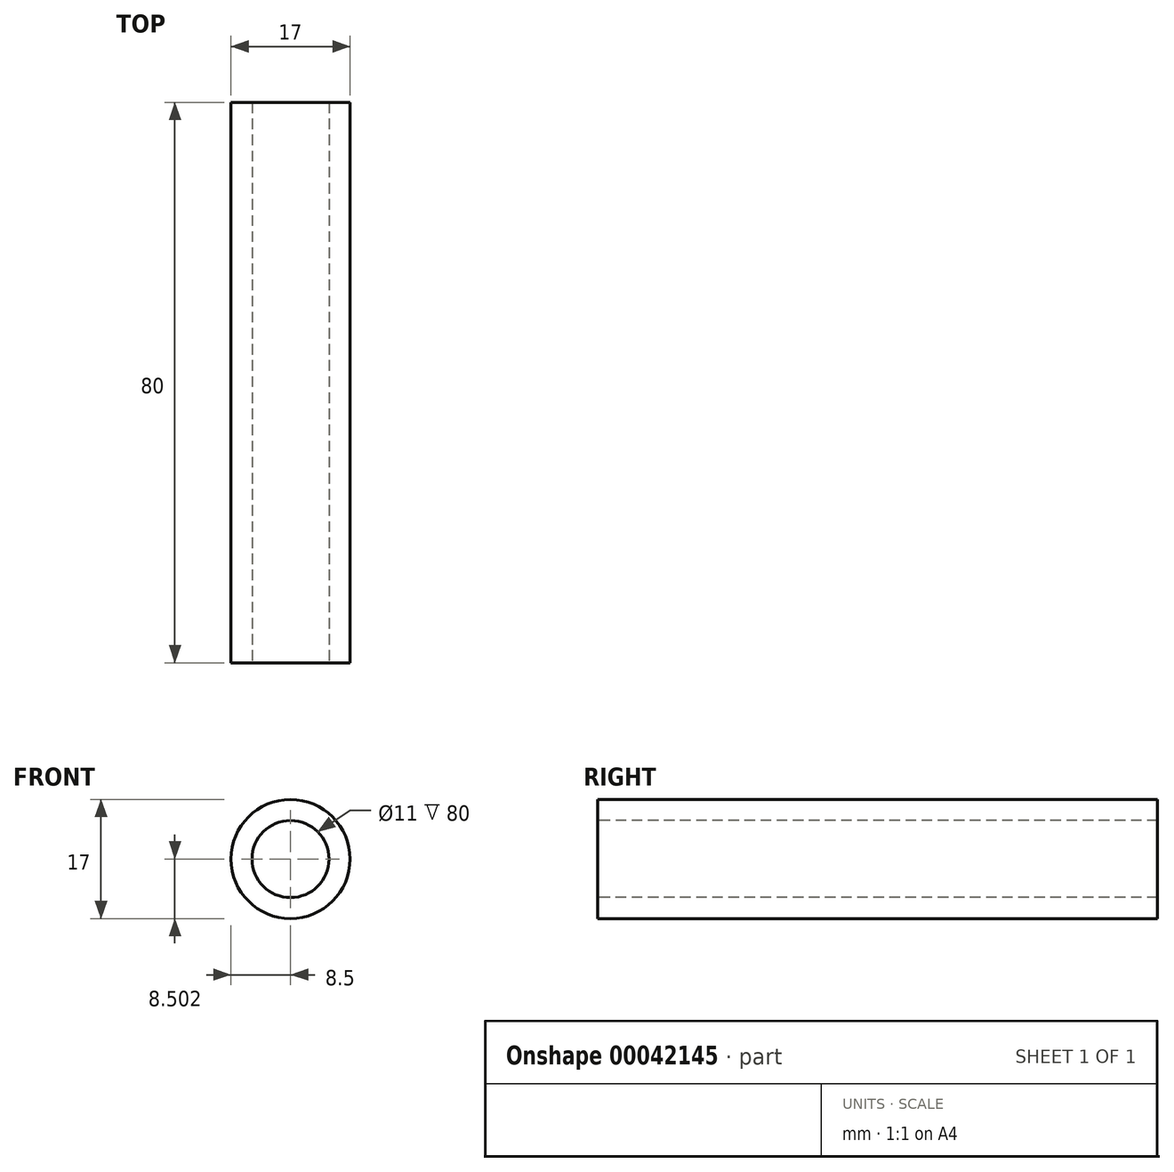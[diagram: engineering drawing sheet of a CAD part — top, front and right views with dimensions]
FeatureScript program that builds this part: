
annotation { "Feature Type Name" : "Feature", "Feature Type Description" : "" }
export const myFeature = defineFeature(function(context is Context, id is Id, definition is map)
    precondition{}
    {
        {
            var Q0;
            Q0=qCreatedBy(makeId("Right.planeOp"),FACE);
            var sketch = newSketch(context, id + "F0", { "sketchPlane" : qUnion([Q0])});
            skLineSegment(sketch, "E0", {"start": v(0, -16.48) * mm, "end": v(78.42, -16.48) * mm, "construction": true});
            skLineSegment(sketch, "E1.bottom", {"start": v(0, -7.98) * mm, "end": v(80, -7.98) * mm});
            skLineSegment(sketch, "E1.top", {"start": v(0, -10.98) * mm, "end": v(80, -10.98) * mm});
            skLineSegment(sketch, "E1.left", {"start": v(0, -7.98) * mm, "end": v(0, -10.98) * mm});
            skLineSegment(sketch, "E1.right", {"start": v(80, -7.98) * mm, "end": v(80, -10.98) * mm});
            skLineSegment(sketch, "E2.MirrorCS", {"start": v(80, -24.98) * mm, "end": v(80, -21.98) * mm});
            skLineSegment(sketch, "E3.MirrorCS", {"start": v(0, -24.98) * mm, "end": v(0, -21.98) * mm});
            skLineSegment(sketch, "E4.MirrorCS", {"start": v(0, -21.98) * mm, "end": v(80, -21.98) * mm});
            skLineSegment(sketch, "E5.MirrorCS", {"start": v(0, -24.98) * mm, "end": v(80, -24.98) * mm});
            skSolve(sketch);
        }
        {
            var Q0;
            Q0=makeQuery(id+"F0.imprint","IMPRINT",FACE,{"disambiguationData":[TD([[makeQuery(id+"F0.imprint","IMPRINT",EDGE,{"derivedFrom":sQuery(id+"F0.wireOp",EDGE,"E1.bottom")}),-1.0]])]});
            var Q1;
            Q1=sQuery(id+"F0.wireOp",EDGE,"E0");
            revolve(context, id + "F1", {"entities" : qUnion([Q0]), "axis" : qUnion([Q1]), "revolveType" : RevolveType.FULL});
        }
    });
